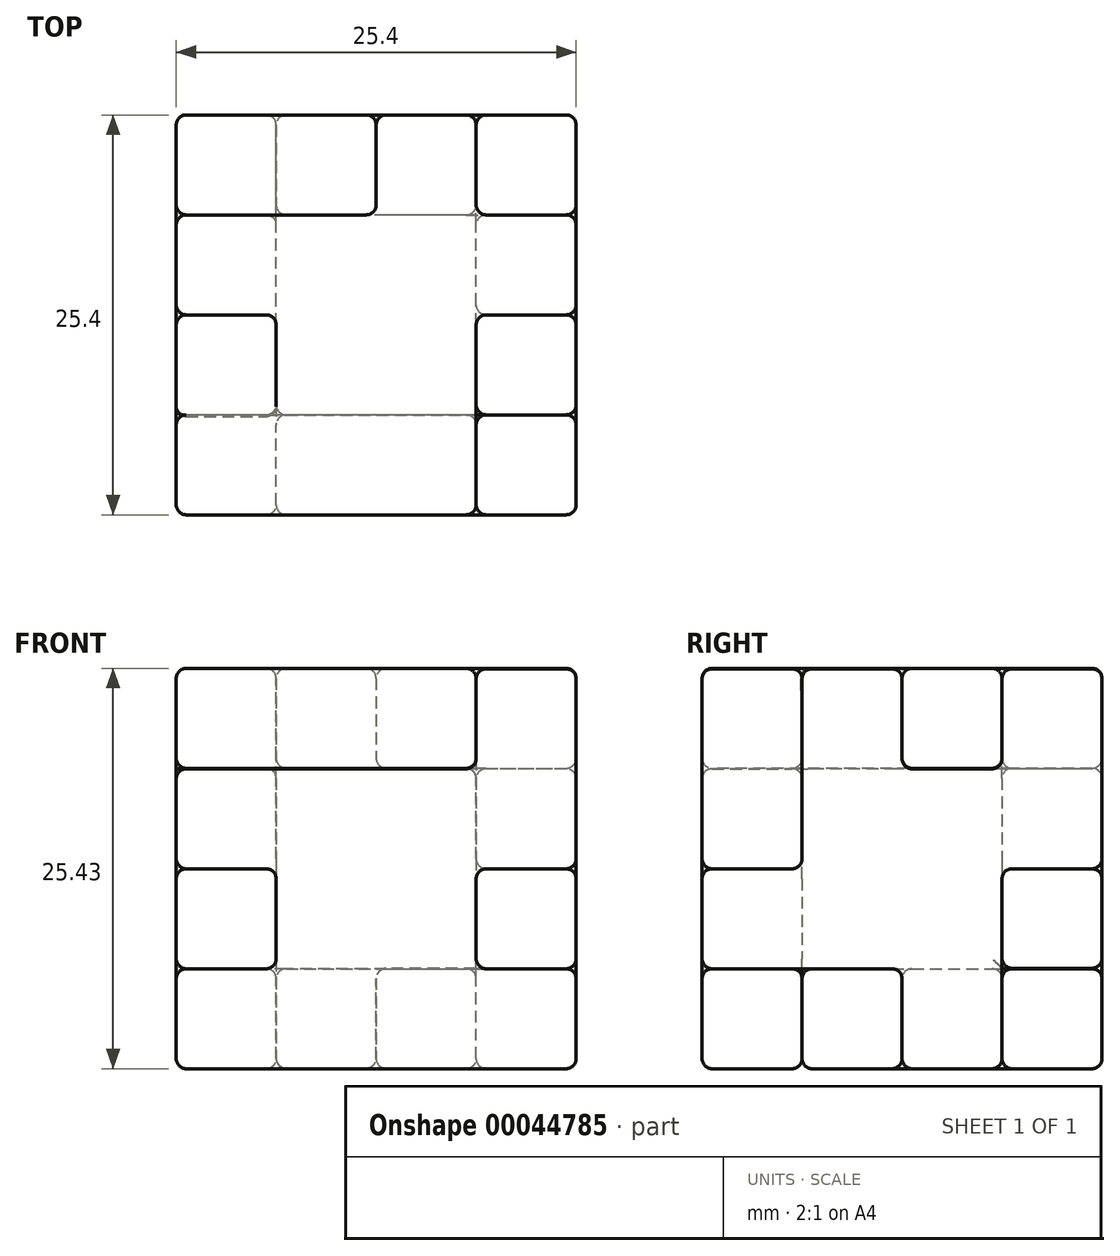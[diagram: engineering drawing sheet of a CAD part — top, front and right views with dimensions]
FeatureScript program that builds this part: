
annotation { "Feature Type Name" : "Feature", "Feature Type Description" : "" }
export const myFeature = defineFeature(function(context is Context, id is Id, definition is map)
    precondition{}
    {
        {
            var Q0;
            Q0=qCreatedBy(makeId("Front.planeOp"),FACE);
            var sketch = newSketch(context, id + "F0", { "sketchPlane" : qUnion([Q0])});
            skLineSegment(sketch, "E0", {"start": v(0, 12.73) * mm, "end": v(0, 6.38) * mm});
            skLineSegment(sketch, "E1.rect.bottom", {"start": v(6.35, 6.38) * mm, "end": v(0, 6.38) * mm});
            skLineSegment(sketch, "E1.rect.top", {"start": v(6.35, -6.32) * mm, "end": v(0, -6.32) * mm});
            skLineSegment(sketch, "E1.rect.left", {"start": v(6.35, 6.38) * mm, "end": v(6.35, 0) * mm});
            skLineSegment(sketch, "E1.rect.right", {"start": v(-6.35, 6.38) * mm, "end": v(-6.35, -6.32) * mm});
            skPoint(sketch, "E1.rect.middle", {"position": v(0, 0.03) * mm});
            skLineSegment(sketch, "E2", {"start": v(-6.35, 6.38) * mm, "end": v(-12.7, 6.38) * mm});
            skLineSegment(sketch, "E3", {"start": v(0, 6.38) * mm, "end": v(0, 12.73) * mm});
            skLineSegment(sketch, "E4", {"start": v(0, 12.73) * mm, "end": v(-12.67, 12.73) * mm});
            skLineSegment(sketch, "E5", {"start": v(-12.67, 12.73) * mm, "end": v(-12.7, 6.38) * mm});
            skLineSegment(sketch, "E6", {"start": v(6.35, -6.32) * mm, "end": v(12.7, -6.32) * mm});
            skLineSegment(sketch, "E7", {"start": v(12.7, 0) * mm, "end": v(12.7, -6.32) * mm});
            skLineSegment(sketch, "E8", {"start": v(12.7, 0) * mm, "end": v(6.35, 0) * mm});
            skLineSegment(sketch, "E9.trimOffspring", {"start": v(6.35, 0) * mm, "end": v(12.7, 0) * mm});
            skPoint(sketch, "E10.orphan", {"position": v(0, 22.29) * mm});
            skPoint(sketch, "E11.trimOffspring.end.orphan", {"position": v(0, -22.23) * mm});
            skPoint(sketch, "E12.start.orphan", {"position": v(-22.35, 0) * mm});
            skLineSegment(sketch, "E13", {"start": v(-6.35, -6.32) * mm, "end": v(-6.35, -12.67) * mm});
            skLineSegment(sketch, "E14", {"start": v(0, -6.32) * mm, "end": v(0, -12.67) * mm});
            skLineSegment(sketch, "E15", {"start": v(0, -12.67) * mm, "end": v(-6.35, -12.67) * mm});
            skSolve(sketch);
        }
        {
            var Q0;
            Q0 = qSketchRegion(id + "F0", true);
            extrude(context, id + "F1", {"entities" : qUnion([Q0]), "oppositeDirection" : true, "depth" : 6.35 * mm});
        }
        {
            var Q0;
            Q0=makeQuery(id+"F1.opExtrude","SWEPT_FACE",FACE,{"disambiguationData":[OSD([sQuery(id+"F0.wireOp",EDGE,"E1.rect.right"),sQuery(id+"F0.wireOp",EDGE,"E13")])]});
            var sketch = newSketch(context, id + "F2", { "sketchPlane" : qUnion([Q0])});
            skLineSegment(sketch, "E16", {"start": v(0, -12.67) * mm, "end": v(0, -6.32) * mm});
            skLineSegment(sketch, "E17.bottom", {"start": v(0, -6.32) * mm, "end": v(-6.35, -6.32) * mm});
            skLineSegment(sketch, "E17.top", {"start": v(0, 6.38) * mm, "end": v(-6.35, 6.38) * mm});
            skLineSegment(sketch, "E17.right", {"start": v(-6.35, -6.32) * mm, "end": v(-6.35, 6.38) * mm});
            skLineSegment(sketch, "E18", {"start": v(6.35, 6.38) * mm, "end": v(0, 6.38) * mm});
            skLineSegment(sketch, "E19", {"start": v(6.35, -6.35) * mm, "end": v(0, -6.35) * mm});
            skLineSegment(sketch, "E20.right", {"start": v(12.7, 0) * mm, "end": v(12.7, 6.35) * mm});
            skLineSegment(sketch, "E21", {"start": v(6.35, 6.38) * mm, "end": v(6.35, 12.73) * mm});
            skLineSegment(sketch, "E22", {"start": v(6.35, 12.73) * mm, "end": v(12.81, 12.73) * mm});
            skLineSegment(sketch, "E23", {"start": v(12.81, 12.73) * mm, "end": v(12.7, 6.35) * mm});
            skLineSegment(sketch, "E24", {"start": v(6.35, -12.7) * mm, "end": v(6.35, -6.35) * mm});
            skLineSegment(sketch, "E25", {"start": v(12.7, -12.7) * mm, "end": v(6.35, -12.7) * mm});
            skLineSegment(sketch, "E26", {"start": v(12.7, -6.35) * mm, "end": v(12.7, -12.7) * mm});
            skLineSegment(sketch, "E27", {"start": v(12.7, -6.35) * mm, "end": v(19.05, -6.35) * mm});
            skLineSegment(sketch, "E28", {"start": v(19.05, -6.35) * mm, "end": v(19.05, 0) * mm});
            skLineSegment(sketch, "E29", {"start": v(19.05, 0) * mm, "end": v(12.7, 0) * mm});
            skLineSegment(sketch, "E30", {"start": v(6.35, 6.38) * mm, "end": v(6.35, 6.35) * mm});
            skSolve(sketch);
        }
        {
            var Q0;
            Q0 = qSketchRegion(id + "F2", true);
            extrude(context, id + "F3", {"entities" : qUnion([Q0]), "depth" : 6.35 * mm});
        }
        {
            var Q0;
            Q0=makeQuery(id+"F3.opExtrude","SWEPT_FACE",FACE,{"disambiguationData":[OSD([sQuery(id+"F2.wireOp",EDGE,"E19")])]});
            var sketch = newSketch(context, id + "F4", { "sketchPlane" : qUnion([Q0])});
            skLineSegment(sketch, "E31", {"start": v(-12.7, 6.35) * mm, "end": v(-12.7, -6.35) * mm});
            skLineSegment(sketch, "E32", {"start": v(-12.7, -6.35) * mm, "end": v(-6.35, -6.35) * mm});
            skLineSegment(sketch, "E33", {"start": v(-6.35, -6.35) * mm, "end": v(-6.35, 0) * mm});
            skLineSegment(sketch, "E34", {"start": v(-6.35, 6.35) * mm, "end": v(-12.7, 6.35) * mm});
            skLineSegment(sketch, "E35", {"start": v(0, 0) * mm, "end": v(-6.35, 0) * mm});
            skLineSegment(sketch, "E36", {"start": v(-6.35, 0) * mm, "end": v(0, 0) * mm});
            skLineSegment(sketch, "E37", {"start": v(-6.35, 6.35) * mm, "end": v(-6.35, 12.7) * mm});
            skLineSegment(sketch, "E38", {"start": v(-6.35, 12.7) * mm, "end": v(12.7, 12.7) * mm});
            skLineSegment(sketch, "E39", {"start": v(12.7, 12.7) * mm, "end": v(12.7, 6.35) * mm});
            skLineSegment(sketch, "E40", {"start": v(12.7, 6.35) * mm, "end": v(6.35, 6.35) * mm});
            skLineSegment(sketch, "E41", {"start": v(6.35, 6.35) * mm, "end": v(6.35, 0) * mm});
            skLineSegment(sketch, "E42", {"start": v(6.35, 0) * mm, "end": v(12.7, 0) * mm});
            skLineSegment(sketch, "E43", {"start": v(0, 0) * mm, "end": v(0, -6.35) * mm});
            skLineSegment(sketch, "E44", {"start": v(0, -6.35) * mm, "end": v(12.7, -6.35) * mm});
            skLineSegment(sketch, "E45", {"start": v(12.7, -6.35) * mm, "end": v(12.7, 0) * mm});
            skPoint(sketch, "E46.start.orphan", {"position": v(0, 6.35) * mm});
            skLineSegment(sketch, "E47", {"start": v(-12.7, 6.35) * mm, "end": v(-6.35, 6.35) * mm, "construction": true});
            skLineSegment(sketch, "E48", {"start": v(-6.35, 0) * mm, "end": v(-6.35, -6.35) * mm, "construction": true});
            skSolve(sketch);
        }
        {
            var Q0;
            Q0 = qSketchRegion(id + "F4", true);
            extrude(context, id + "F5", {"entities" : qUnion([Q0]), "depth" : 6.35 * mm});
        }
        {
            var Q0;
            Q0=makeQuery(id+"F5.opExtrude","SWEPT_FACE",FACE,{"disambiguationData":[OSD([sQuery(id+"F4.wireOp",EDGE,"E41")])]});
            var sketch = newSketch(context, id + "F6", { "sketchPlane" : qUnion([Q0])});
            skLineSegment(sketch, "E49", {"start": v(0, -12.7) * mm, "end": v(-6.35, -12.7) * mm});
            skLineSegment(sketch, "E50", {"start": v(-6.35, -12.7) * mm, "end": v(-6.35, -6.35) * mm});
            skLineSegment(sketch, "E51", {"start": v(-6.35, -6.35) * mm, "end": v(-19.05, -6.35) * mm});
            skLineSegment(sketch, "E52", {"start": v(-19.05, -6.35) * mm, "end": v(-19.05, 0) * mm});
            skLineSegment(sketch, "E53", {"start": v(-19.05, 0) * mm, "end": v(-12.7, 0) * mm});
            skLineSegment(sketch, "E54", {"start": v(-12.7, 0) * mm, "end": v(-12.7, 12.7) * mm});
            skLineSegment(sketch, "E55", {"start": v(-12.7, 12.7) * mm, "end": v(-6.35, 12.7) * mm});
            skLineSegment(sketch, "E56", {"start": v(-6.35, 12.7) * mm, "end": v(-6.35, 6.35) * mm});
            skLineSegment(sketch, "E57", {"start": v(0, -12.7) * mm, "end": v(0, 0) * mm});
            skLineSegment(sketch, "E58", {"start": v(0, 0) * mm, "end": v(6.35, 0) * mm});
            skLineSegment(sketch, "E59", {"start": v(-6.35, 6.35) * mm, "end": v(0, 6.35) * mm});
            skLineSegment(sketch, "E60", {"start": v(0, 6.35) * mm, "end": v(0, 12.7) * mm});
            skLineSegment(sketch, "E61", {"start": v(6.35, 0) * mm, "end": v(6.35, 12.7) * mm});
            skLineSegment(sketch, "E62", {"start": v(6.35, 12.7) * mm, "end": v(0, 12.7) * mm});
            skSolve(sketch);
        }
        {
            var Q0;
            Q0 = qSketchRegion(id + "F6", true);
            extrude(context, id + "F7", {"entities" : qUnion([Q0]), "depth" : 6.35 * mm});
        }
        {
            var Q0;
            Q0=makeQuery(id+"F1.opExtrude","SWEPT_FACE",FACE,{"disambiguationData":[OSD([sQuery(id+"F0.wireOp",EDGE,"E1.rect.bottom")])]});
            var sketch = newSketch(context, id + "F8", { "sketchPlane" : qUnion([Q0])});
            skLineSegment(sketch, "E63", {"start": v(6.35, 6.35) * mm, "end": v(6.35, 0) * mm});
            skLineSegment(sketch, "E64", {"start": v(6.35, 0) * mm, "end": v(12.7, 0) * mm});
            skLineSegment(sketch, "E65", {"start": v(12.7, 0) * mm, "end": v(12.7, -6.35) * mm});
            skLineSegment(sketch, "E66", {"start": v(12.7, -6.35) * mm, "end": v(6.35, -6.35) * mm});
            skLineSegment(sketch, "E67", {"start": v(6.35, -6.35) * mm, "end": v(6.35, -19.05) * mm});
            skLineSegment(sketch, "E68", {"start": v(6.35, -19.05) * mm, "end": v(-12.7, -19.05) * mm});
            skLineSegment(sketch, "E69", {"start": v(-12.7, -19.05) * mm, "end": v(-12.7, -12.7) * mm});
            skLineSegment(sketch, "E70", {"start": v(-12.7, -12.7) * mm, "end": v(-6.35, -12.7) * mm});
            skLineSegment(sketch, "E71", {"start": v(-6.35, -12.7) * mm, "end": v(-6.35, -6.35) * mm});
            skLineSegment(sketch, "E72", {"start": v(-6.35, -6.35) * mm, "end": v(-12.7, -6.35) * mm});
            skLineSegment(sketch, "E73", {"start": v(-12.7, -6.35) * mm, "end": v(-12.7, 0) * mm});
            skLineSegment(sketch, "E74", {"start": v(-12.7, 0) * mm, "end": v(0, 0) * mm});
            skLineSegment(sketch, "E75", {"start": v(0, 0) * mm, "end": v(0, 6.35) * mm});
            skLineSegment(sketch, "E76", {"start": v(0, 6.35) * mm, "end": v(6.35, 6.35) * mm});
            skSolve(sketch);
        }
        {
            var Q0;
            Q0 = qSketchRegion(id + "F8", true);
            extrude(context, id + "F9", {"entities" : qUnion([Q0]), "depth" : 6.35 * mm});
        }
        {
            var Q0;
            Q0=makeQuery(id+"F5.opExtrude","SWEPT_FACE",FACE,{"disambiguationData":[OSD([sQuery(id+"F4.wireOp",EDGE,"E38")])]});
            var sketch = newSketch(context, id + "F10", { "sketchPlane" : qUnion([Q0])});
            skLineSegment(sketch, "E77", {"start": v(12.7, -12.7) * mm, "end": v(-12.7, -12.7) * mm});
            skLineSegment(sketch, "E78", {"start": v(12.7, -12.7) * mm, "end": v(12.7, -6.35) * mm});
            skLineSegment(sketch, "E79", {"start": v(12.7, -6.35) * mm, "end": v(6.35, -6.35) * mm});
            skLineSegment(sketch, "E80", {"start": v(6.35, -6.35) * mm, "end": v(6.35, 0) * mm});
            skLineSegment(sketch, "E81", {"start": v(6.35, 0) * mm, "end": v(12.7, 0) * mm});
            skLineSegment(sketch, "E82", {"start": v(12.7, 0) * mm, "end": v(12.7, 12.7) * mm});
            skLineSegment(sketch, "E83", {"start": v(12.7, 12.7) * mm, "end": v(6.35, 12.7) * mm});
            skLineSegment(sketch, "E84", {"start": v(6.35, 12.7) * mm, "end": v(6.35, 6.35) * mm});
            skLineSegment(sketch, "E85", {"start": v(6.35, 6.35) * mm, "end": v(-12.7, 6.35) * mm});
            skLineSegment(sketch, "E86", {"start": v(-12.7, 6.35) * mm, "end": v(-12.7, 0) * mm});
            skLineSegment(sketch, "E87", {"start": v(-12.7, 0) * mm, "end": v(-6.35, 0) * mm});
            skLineSegment(sketch, "E88", {"start": v(-6.35, 0) * mm, "end": v(-6.35, -6.35) * mm});
            skLineSegment(sketch, "E89", {"start": v(-6.35, -6.35) * mm, "end": v(-12.7, -6.35) * mm});
            skLineSegment(sketch, "E90", {"start": v(-12.7, -6.35) * mm, "end": v(-12.7, -12.7) * mm});
            skSolve(sketch);
        }
        {
            var Q0;
            Q0 = qSketchRegion(id + "F10", true);
            extrude(context, id + "F11", {"entities" : qUnion([Q0]), "depth" : 6.35 * mm});
        }
        {
            var Q0;
            Q0=makeQuery(id+"F1.opExtrude","CAP_FACE",FACE,{"disambiguationData":[OSD([sQuery(id+"F0.wireOp",EDGE,"E1.rect.bottom"),sQuery(id+"F0.wireOp",EDGE,"E1.rect.top"),sQuery(id+"F0.wireOp",EDGE,"E1.rect.left"),sQuery(id+"F0.wireOp",EDGE,"E1.rect.right"),sQuery(id+"F0.wireOp",EDGE,"E2"),sQuery(id+"F0.wireOp",EDGE,"E3"),sQuery(id+"F0.wireOp",EDGE,"E4"),sQuery(id+"F0.wireOp",EDGE,"E5"),sQuery(id+"F0.wireOp",EDGE,"E6"),sQuery(id+"F0.wireOp",EDGE,"E7"),sQuery(id+"F0.wireOp",EDGE,"E9.trimOffspring"),sQuery(id+"F0.wireOp",EDGE,"E13"),sQuery(id+"F0.wireOp",EDGE,"E14"),sQuery(id+"F0.wireOp",EDGE,"E15")])],"isStart":false});
            var Q1;
            Q1=makeQuery(id+"F1.opExtrude","CAP_FACE",FACE,{"disambiguationData":[OSD([sQuery(id+"F0.wireOp",EDGE,"E1.rect.bottom"),sQuery(id+"F0.wireOp",EDGE,"E1.rect.top"),sQuery(id+"F0.wireOp",EDGE,"E1.rect.left"),sQuery(id+"F0.wireOp",EDGE,"E1.rect.right"),sQuery(id+"F0.wireOp",EDGE,"E2"),sQuery(id+"F0.wireOp",EDGE,"E3"),sQuery(id+"F0.wireOp",EDGE,"E4"),sQuery(id+"F0.wireOp",EDGE,"E5"),sQuery(id+"F0.wireOp",EDGE,"E6"),sQuery(id+"F0.wireOp",EDGE,"E7"),sQuery(id+"F0.wireOp",EDGE,"E9.trimOffspring"),sQuery(id+"F0.wireOp",EDGE,"E13"),sQuery(id+"F0.wireOp",EDGE,"E14"),sQuery(id+"F0.wireOp",EDGE,"E15")])],"isStart":true});
            var Q2;
            Q2=makeQuery(id+"F1.opExtrude","SWEPT_EDGE",EDGE,{"disambiguationData":[OSD([sQuery(id+"F0.wireOp",EDGE,"E3"),sQuery(id+"F0.wireOp",EDGE,"E4")])]});
            var Q3;
            Q3=makeQuery(id+"F1.opExtrude","SWEPT_EDGE",EDGE,{"disambiguationData":[OSD([sQuery(id+"F0.wireOp",EDGE,"E1.rect.bottom"),sQuery(id+"F0.wireOp",EDGE,"E3")])]});
            var Q4;
            Q4=makeQuery(id+"F1.opExtrude","SWEPT_EDGE",EDGE,{"disambiguationData":[OSD([sQuery(id+"F0.wireOp",EDGE,"E1.rect.bottom"),sQuery(id+"F0.wireOp",EDGE,"E1.rect.left")])]});
            var Q5;
            Q5=makeQuery(id+"F1.opExtrude","SWEPT_EDGE",EDGE,{"disambiguationData":[OSD([sQuery(id+"F0.wireOp",EDGE,"E1.rect.left"),sQuery(id+"F0.wireOp",EDGE,"E9.trimOffspring")])]});
            var Q6;
            Q6=makeQuery(id+"F1.opExtrude","SWEPT_EDGE",EDGE,{"disambiguationData":[OSD([sQuery(id+"F0.wireOp",EDGE,"E7"),sQuery(id+"F0.wireOp",EDGE,"E9.trimOffspring")])]});
            var Q7;
            Q7=makeQuery(id+"F1.opExtrude","SWEPT_EDGE",EDGE,{"disambiguationData":[OSD([sQuery(id+"F0.wireOp",EDGE,"E6"),sQuery(id+"F0.wireOp",EDGE,"E7")])]});
            var Q8;
            Q8=makeQuery(id+"F1.opExtrude","SWEPT_EDGE",EDGE,{"disambiguationData":[OSD([sQuery(id+"F0.wireOp",EDGE,"E1.rect.top"),sQuery(id+"F0.wireOp",EDGE,"E14")])]});
            var Q9;
            Q9=makeQuery(id+"F1.opExtrude","SWEPT_EDGE",EDGE,{"disambiguationData":[OSD([sQuery(id+"F0.wireOp",EDGE,"E14"),sQuery(id+"F0.wireOp",EDGE,"E15")])]});
            var Q10;
            Q10=makeQuery(id+"F1.opExtrude","SWEPT_EDGE",EDGE,{"disambiguationData":[OSD([sQuery(id+"F0.wireOp",EDGE,"E13"),sQuery(id+"F0.wireOp",EDGE,"E15")])]});
            var Q11;
            Q11=makeQuery(id+"F1.opExtrude","SWEPT_EDGE",EDGE,{"disambiguationData":[OSD([sQuery(id+"F0.wireOp",EDGE,"E1.rect.right"),sQuery(id+"F0.wireOp",EDGE,"E2")])]});
            var Q12;
            Q12=makeQuery(id+"F1.opExtrude","SWEPT_EDGE",EDGE,{"disambiguationData":[OSD([sQuery(id+"F0.wireOp",EDGE,"E2"),sQuery(id+"F0.wireOp",EDGE,"E5")])]});
            var Q13;
            Q13=makeQuery(id+"F1.opExtrude","SWEPT_EDGE",EDGE,{"disambiguationData":[OSD([sQuery(id+"F0.wireOp",EDGE,"E4"),sQuery(id+"F0.wireOp",EDGE,"E5")])]});
            var Q14;
            Q14=makeQuery(id+"F3.opExtrude","CAP_FACE",FACE,{"disambiguationData":[OSD([sQuery(id+"F2.wireOp",EDGE,"E16"),sQuery(id+"F2.wireOp",EDGE,"E17.bottom"),sQuery(id+"F2.wireOp",EDGE,"E17.top"),sQuery(id+"F2.wireOp",EDGE,"E17.right"),sQuery(id+"F2.wireOp",EDGE,"E18"),sQuery(id+"F2.wireOp",EDGE,"E19"),sQuery(id+"F2.wireOp",EDGE,"E20.right"),sQuery(id+"F2.wireOp",EDGE,"E21"),sQuery(id+"F2.wireOp",EDGE,"E22"),sQuery(id+"F2.wireOp",EDGE,"E23"),sQuery(id+"F2.wireOp",EDGE,"E24"),sQuery(id+"F2.wireOp",EDGE,"E25"),sQuery(id+"F2.wireOp",EDGE,"E26"),sQuery(id+"F2.wireOp",EDGE,"E27"),sQuery(id+"F2.wireOp",EDGE,"E28"),sQuery(id+"F2.wireOp",EDGE,"E29")])],"isStart":false});
            var Q15;
            Q15=makeQuery(id+"F3.opExtrude","CAP_FACE",FACE,{"disambiguationData":[OSD([sQuery(id+"F2.wireOp",EDGE,"E16"),sQuery(id+"F2.wireOp",EDGE,"E17.bottom"),sQuery(id+"F2.wireOp",EDGE,"E17.top"),sQuery(id+"F2.wireOp",EDGE,"E17.right"),sQuery(id+"F2.wireOp",EDGE,"E18"),sQuery(id+"F2.wireOp",EDGE,"E19"),sQuery(id+"F2.wireOp",EDGE,"E20.right"),sQuery(id+"F2.wireOp",EDGE,"E21"),sQuery(id+"F2.wireOp",EDGE,"E22"),sQuery(id+"F2.wireOp",EDGE,"E23"),sQuery(id+"F2.wireOp",EDGE,"E24"),sQuery(id+"F2.wireOp",EDGE,"E25"),sQuery(id+"F2.wireOp",EDGE,"E26"),sQuery(id+"F2.wireOp",EDGE,"E27"),sQuery(id+"F2.wireOp",EDGE,"E28"),sQuery(id+"F2.wireOp",EDGE,"E29")])],"isStart":true});
            var Q16;
            Q16=makeQuery(id+"F3.opExtrude","SWEPT_EDGE",EDGE,{"disambiguationData":[OSD([sQuery(id+"F2.wireOp",EDGE,"E24"),sQuery(id+"F2.wireOp",EDGE,"E25")])]});
            var Q17;
            Q17=makeQuery(id+"F3.opExtrude","SWEPT_EDGE",EDGE,{"disambiguationData":[OSD([sQuery(id+"F2.wireOp",EDGE,"E25"),sQuery(id+"F2.wireOp",EDGE,"E26")])]});
            var Q18;
            Q18=makeQuery(id+"F3.opExtrude","SWEPT_EDGE",EDGE,{"disambiguationData":[OSD([sQuery(id+"F2.wireOp",EDGE,"E19"),sQuery(id+"F2.wireOp",EDGE,"E24")])]});
            var Q19;
            Q19=makeQuery(id+"F3.opExtrude","SWEPT_EDGE",EDGE,{"disambiguationData":[OSD([sQuery(id+"F0.wireOp",EDGE,"E1.rect.right"),sQuery(id+"F0.wireOp",EDGE,"E13"),sQuery(id+"F2.wireOp",EDGE,"E17.bottom"),sQuery(id+"F2.wireOp",EDGE,"E17.right")])]});
            var Q20;
            Q20=makeQuery(id+"F3.opExtrude","SWEPT_EDGE",EDGE,{"disambiguationData":[OSD([sQuery(id+"F2.wireOp",EDGE,"E17.top"),sQuery(id+"F2.wireOp",EDGE,"E17.right")])]});
            var Q21;
            Q21=makeQuery(id+"F3.opExtrude","SWEPT_EDGE",EDGE,{"disambiguationData":[OSD([sQuery(id+"F2.wireOp",EDGE,"E18"),sQuery(id+"F2.wireOp",EDGE,"E21")])]});
            var Q22;
            Q22=makeQuery(id+"F3.opExtrude","SWEPT_EDGE",EDGE,{"disambiguationData":[OSD([sQuery(id+"F2.wireOp",EDGE,"E21"),sQuery(id+"F2.wireOp",EDGE,"E22")])]});
            var Q23;
            Q23=makeQuery(id+"F3.opExtrude","SWEPT_EDGE",EDGE,{"disambiguationData":[OSD([sQuery(id+"F2.wireOp",EDGE,"E22"),sQuery(id+"F2.wireOp",EDGE,"E23")])]});
            var Q24;
            Q24=makeQuery(id+"F3.opExtrude","SWEPT_EDGE",EDGE,{"disambiguationData":[OSD([sQuery(id+"F2.wireOp",EDGE,"E28"),sQuery(id+"F2.wireOp",EDGE,"E29")])]});
            var Q25;
            Q25=makeQuery(id+"F3.opExtrude","SWEPT_EDGE",EDGE,{"disambiguationData":[OSD([sQuery(id+"F2.wireOp",EDGE,"E20.right"),sQuery(id+"F2.wireOp",EDGE,"E29")])]});
            var Q26;
            Q26=makeQuery(id+"F3.opExtrude","SWEPT_EDGE",EDGE,{"disambiguationData":[OSD([sQuery(id+"F2.wireOp",EDGE,"E27"),sQuery(id+"F2.wireOp",EDGE,"E28")])]});
            var Q27;
            Q27=makeQuery(id+"F3.opExtrude","SWEPT_EDGE",EDGE,{"disambiguationData":[OSD([sQuery(id+"F2.wireOp",EDGE,"E26"),sQuery(id+"F2.wireOp",EDGE,"E27")])]});
            var Q28;
            Q28=makeQuery(id+"F5.opExtrude","CAP_FACE",FACE,{"disambiguationData":[OSD([sQuery(id+"F4.wireOp",EDGE,"E31"),sQuery(id+"F4.wireOp",EDGE,"E32"),sQuery(id+"F4.wireOp",EDGE,"E33"),sQuery(id+"F4.wireOp",EDGE,"E34"),sQuery(id+"F4.wireOp",EDGE,"E36"),sQuery(id+"F4.wireOp",EDGE,"E37"),sQuery(id+"F4.wireOp",EDGE,"E38"),sQuery(id+"F4.wireOp",EDGE,"E39"),sQuery(id+"F4.wireOp",EDGE,"E40"),sQuery(id+"F4.wireOp",EDGE,"E41"),sQuery(id+"F4.wireOp",EDGE,"E42"),sQuery(id+"F4.wireOp",EDGE,"E43"),sQuery(id+"F4.wireOp",EDGE,"E44"),sQuery(id+"F4.wireOp",EDGE,"E45")])],"isStart":false});
            var Q29;
            Q29=makeQuery(id+"F5.opExtrude","CAP_FACE",FACE,{"disambiguationData":[OSD([sQuery(id+"F4.wireOp",EDGE,"E31"),sQuery(id+"F4.wireOp",EDGE,"E32"),sQuery(id+"F4.wireOp",EDGE,"E33"),sQuery(id+"F4.wireOp",EDGE,"E34"),sQuery(id+"F4.wireOp",EDGE,"E36"),sQuery(id+"F4.wireOp",EDGE,"E37"),sQuery(id+"F4.wireOp",EDGE,"E38"),sQuery(id+"F4.wireOp",EDGE,"E39"),sQuery(id+"F4.wireOp",EDGE,"E40"),sQuery(id+"F4.wireOp",EDGE,"E41"),sQuery(id+"F4.wireOp",EDGE,"E42"),sQuery(id+"F4.wireOp",EDGE,"E43"),sQuery(id+"F4.wireOp",EDGE,"E44"),sQuery(id+"F4.wireOp",EDGE,"E45")])],"isStart":true});
            var Q30;
            Q30=makeQuery(id+"F5.opExtrude","SWEPT_EDGE",EDGE,{"disambiguationData":[OSD([sQuery(id+"F4.wireOp",EDGE,"E32"),sQuery(id+"F4.wireOp",EDGE,"E33")])]});
            var Q31;
            Q31=makeQuery(id+"F5.opExtrude","SWEPT_EDGE",EDGE,{"disambiguationData":[OSD([sQuery(id+"F2.wireOp",EDGE,"E16"),sQuery(id+"F2.wireOp",EDGE,"E19"),sQuery(id+"F4.wireOp",EDGE,"E33"),sQuery(id+"F4.wireOp",EDGE,"E36")])]});
            var Q32;
            Q32=makeQuery(id+"F5.opExtrude","SWEPT_EDGE",EDGE,{"disambiguationData":[OSD([sQuery(id+"F4.wireOp",EDGE,"E31"),sQuery(id+"F4.wireOp",EDGE,"E32")])]});
            var Q33;
            Q33=makeQuery(id+"F5.opExtrude","SWEPT_EDGE",EDGE,{"disambiguationData":[OSD([sQuery(id+"F4.wireOp",EDGE,"E36"),sQuery(id+"F4.wireOp",EDGE,"E43")])]});
            var Q34;
            Q34=makeQuery(id+"F5.opExtrude","SWEPT_EDGE",EDGE,{"disambiguationData":[OSD([sQuery(id+"F4.wireOp",EDGE,"E43"),sQuery(id+"F4.wireOp",EDGE,"E44")])]});
            var Q35;
            Q35=makeQuery(id+"F5.opExtrude","SWEPT_EDGE",EDGE,{"disambiguationData":[OSD([sQuery(id+"F4.wireOp",EDGE,"E44"),sQuery(id+"F4.wireOp",EDGE,"E45")])]});
            var Q36;
            Q36=makeQuery(id+"F5.opExtrude","SWEPT_EDGE",EDGE,{"disambiguationData":[OSD([sQuery(id+"F4.wireOp",EDGE,"E42"),sQuery(id+"F4.wireOp",EDGE,"E45")])]});
            var Q37;
            Q37=makeQuery(id+"F5.opExtrude","SWEPT_EDGE",EDGE,{"disambiguationData":[OSD([sQuery(id+"F4.wireOp",EDGE,"E41"),sQuery(id+"F4.wireOp",EDGE,"E42")])]});
            var Q38;
            Q38=makeQuery(id+"F5.opExtrude","SWEPT_EDGE",EDGE,{"disambiguationData":[OSD([sQuery(id+"F4.wireOp",EDGE,"E40"),sQuery(id+"F4.wireOp",EDGE,"E41")])]});
            var Q39;
            Q39=makeQuery(id+"F5.opExtrude","SWEPT_EDGE",EDGE,{"disambiguationData":[OSD([sQuery(id+"F4.wireOp",EDGE,"E39"),sQuery(id+"F4.wireOp",EDGE,"E40")])]});
            var Q40;
            Q40=makeQuery(id+"F5.opExtrude","SWEPT_EDGE",EDGE,{"disambiguationData":[OSD([sQuery(id+"F4.wireOp",EDGE,"E38"),sQuery(id+"F4.wireOp",EDGE,"E39")])]});
            var Q41;
            Q41=makeQuery(id+"F5.opExtrude","SWEPT_EDGE",EDGE,{"disambiguationData":[OSD([sQuery(id+"F4.wireOp",EDGE,"E31"),sQuery(id+"F4.wireOp",EDGE,"E34")])]});
            var Q42;
            Q42=makeQuery(id+"F5.opExtrude","SWEPT_EDGE",EDGE,{"disambiguationData":[OSD([sQuery(id+"F2.wireOp",EDGE,"E19"),sQuery(id+"F4.wireOp",EDGE,"E34"),sQuery(id+"F4.wireOp",EDGE,"E37")])]});
            var Q43;
            Q43=makeQuery(id+"F5.opExtrude","SWEPT_EDGE",EDGE,{"disambiguationData":[OSD([sQuery(id+"F4.wireOp",EDGE,"E37"),sQuery(id+"F4.wireOp",EDGE,"E38")])]});
            var Q44;
            Q44=makeQuery(id+"F7.opExtrude","CAP_FACE",FACE,{"disambiguationData":[OSD([sQuery(id+"F6.wireOp",EDGE,"E49"),sQuery(id+"F6.wireOp",EDGE,"E50"),sQuery(id+"F6.wireOp",EDGE,"E51"),sQuery(id+"F6.wireOp",EDGE,"E52"),sQuery(id+"F6.wireOp",EDGE,"E53"),sQuery(id+"F6.wireOp",EDGE,"E54"),sQuery(id+"F6.wireOp",EDGE,"E55"),sQuery(id+"F6.wireOp",EDGE,"E56"),sQuery(id+"F6.wireOp",EDGE,"E57"),sQuery(id+"F6.wireOp",EDGE,"E58"),sQuery(id+"F6.wireOp",EDGE,"E59"),sQuery(id+"F6.wireOp",EDGE,"E60"),sQuery(id+"F6.wireOp",EDGE,"E61"),sQuery(id+"F6.wireOp",EDGE,"E62")])],"isStart":false});
            var Q45;
            Q45=makeQuery(id+"F7.opExtrude","CAP_FACE",FACE,{"disambiguationData":[OSD([sQuery(id+"F6.wireOp",EDGE,"E49"),sQuery(id+"F6.wireOp",EDGE,"E50"),sQuery(id+"F6.wireOp",EDGE,"E51"),sQuery(id+"F6.wireOp",EDGE,"E52"),sQuery(id+"F6.wireOp",EDGE,"E53"),sQuery(id+"F6.wireOp",EDGE,"E54"),sQuery(id+"F6.wireOp",EDGE,"E55"),sQuery(id+"F6.wireOp",EDGE,"E56"),sQuery(id+"F6.wireOp",EDGE,"E57"),sQuery(id+"F6.wireOp",EDGE,"E58"),sQuery(id+"F6.wireOp",EDGE,"E59"),sQuery(id+"F6.wireOp",EDGE,"E60"),sQuery(id+"F6.wireOp",EDGE,"E61"),sQuery(id+"F6.wireOp",EDGE,"E62")])],"isStart":true});
            var Q46;
            Q46=makeQuery(id+"F7.opExtrude","SWEPT_EDGE",EDGE,{"disambiguationData":[OSD([sQuery(id+"F6.wireOp",EDGE,"E56"),sQuery(id+"F6.wireOp",EDGE,"E59")])]});
            var Q47;
            Q47=makeQuery(id+"F7.opExtrude","SWEPT_EDGE",EDGE,{"disambiguationData":[OSD([sQuery(id+"F6.wireOp",EDGE,"E55"),sQuery(id+"F6.wireOp",EDGE,"E56")])]});
            var Q48;
            Q48=makeQuery(id+"F7.opExtrude","SWEPT_EDGE",EDGE,{"disambiguationData":[OSD([sQuery(id+"F6.wireOp",EDGE,"E54"),sQuery(id+"F6.wireOp",EDGE,"E55")])]});
            var Q49;
            Q49=makeQuery(id+"F7.opExtrude","SWEPT_EDGE",EDGE,{"disambiguationData":[OSD([sQuery(id+"F6.wireOp",EDGE,"E60"),sQuery(id+"F6.wireOp",EDGE,"E62")])]});
            var Q50;
            Q50=makeQuery(id+"F7.opExtrude","SWEPT_EDGE",EDGE,{"disambiguationData":[OSD([sQuery(id+"F6.wireOp",EDGE,"E61"),sQuery(id+"F6.wireOp",EDGE,"E62")])]});
            var Q51;
            Q51=makeQuery(id+"F7.opExtrude","SWEPT_EDGE",EDGE,{"disambiguationData":[OSD([sQuery(id+"F6.wireOp",EDGE,"E58"),sQuery(id+"F6.wireOp",EDGE,"E61")])]});
            var Q52;
            Q52=makeQuery(id+"F7.opExtrude","SWEPT_EDGE",EDGE,{"disambiguationData":[OSD([sQuery(id+"F6.wireOp",EDGE,"E59"),sQuery(id+"F6.wireOp",EDGE,"E60")])]});
            var Q53;
            Q53=makeQuery(id+"F7.opExtrude","SWEPT_EDGE",EDGE,{"disambiguationData":[OSD([sQuery(id+"F6.wireOp",EDGE,"E53"),sQuery(id+"F6.wireOp",EDGE,"E54")])]});
            var Q54;
            Q54=makeQuery(id+"F7.opExtrude","SWEPT_EDGE",EDGE,{"disambiguationData":[OSD([sQuery(id+"F6.wireOp",EDGE,"E52"),sQuery(id+"F6.wireOp",EDGE,"E53")])]});
            var Q55;
            Q55=makeQuery(id+"F7.opExtrude","SWEPT_EDGE",EDGE,{"disambiguationData":[OSD([sQuery(id+"F6.wireOp",EDGE,"E51"),sQuery(id+"F6.wireOp",EDGE,"E52")])]});
            var Q56;
            Q56=makeQuery(id+"F7.opExtrude","SWEPT_EDGE",EDGE,{"disambiguationData":[OSD([sQuery(id+"F6.wireOp",EDGE,"E57"),sQuery(id+"F6.wireOp",EDGE,"E58")])]});
            var Q57;
            Q57=makeQuery(id+"F7.opExtrude","SWEPT_EDGE",EDGE,{"disambiguationData":[OSD([sQuery(id+"F6.wireOp",EDGE,"E49"),sQuery(id+"F6.wireOp",EDGE,"E57")])]});
            var Q58;
            Q58=makeQuery(id+"F7.opExtrude","SWEPT_EDGE",EDGE,{"disambiguationData":[OSD([sQuery(id+"F6.wireOp",EDGE,"E49"),sQuery(id+"F6.wireOp",EDGE,"E50")])]});
            var Q59;
            Q59=makeQuery(id+"F7.opExtrude","SWEPT_EDGE",EDGE,{"disambiguationData":[OSD([sQuery(id+"F4.wireOp",EDGE,"E41"),sQuery(id+"F6.wireOp",EDGE,"E50"),sQuery(id+"F6.wireOp",EDGE,"E51")])]});
            var Q60;
            Q60=makeQuery(id+"F9.opExtrude","CAP_FACE",FACE,{"disambiguationData":[OSD([sQuery(id+"F8.wireOp",EDGE,"E63"),sQuery(id+"F8.wireOp",EDGE,"E64"),sQuery(id+"F8.wireOp",EDGE,"E65"),sQuery(id+"F8.wireOp",EDGE,"E66"),sQuery(id+"F8.wireOp",EDGE,"E67"),sQuery(id+"F8.wireOp",EDGE,"E68"),sQuery(id+"F8.wireOp",EDGE,"E69"),sQuery(id+"F8.wireOp",EDGE,"E70"),sQuery(id+"F8.wireOp",EDGE,"E71"),sQuery(id+"F8.wireOp",EDGE,"E72"),sQuery(id+"F8.wireOp",EDGE,"E73"),sQuery(id+"F8.wireOp",EDGE,"E74"),sQuery(id+"F8.wireOp",EDGE,"E75"),sQuery(id+"F8.wireOp",EDGE,"E76")])],"isStart":true});
            var Q61;
            Q61=makeQuery(id+"F9.opExtrude","CAP_FACE",FACE,{"disambiguationData":[OSD([sQuery(id+"F8.wireOp",EDGE,"E63"),sQuery(id+"F8.wireOp",EDGE,"E64"),sQuery(id+"F8.wireOp",EDGE,"E65"),sQuery(id+"F8.wireOp",EDGE,"E66"),sQuery(id+"F8.wireOp",EDGE,"E67"),sQuery(id+"F8.wireOp",EDGE,"E68"),sQuery(id+"F8.wireOp",EDGE,"E69"),sQuery(id+"F8.wireOp",EDGE,"E70"),sQuery(id+"F8.wireOp",EDGE,"E71"),sQuery(id+"F8.wireOp",EDGE,"E72"),sQuery(id+"F8.wireOp",EDGE,"E73"),sQuery(id+"F8.wireOp",EDGE,"E74"),sQuery(id+"F8.wireOp",EDGE,"E75"),sQuery(id+"F8.wireOp",EDGE,"E76")])],"isStart":false});
            var Q62;
            Q62=makeQuery(id+"F9.opExtrude","SWEPT_EDGE",EDGE,{"disambiguationData":[OSD([sQuery(id+"F8.wireOp",EDGE,"E70"),sQuery(id+"F8.wireOp",EDGE,"E71")])]});
            var Q63;
            Q63=makeQuery(id+"F9.opExtrude","SWEPT_EDGE",EDGE,{"disambiguationData":[OSD([sQuery(id+"F8.wireOp",EDGE,"E69"),sQuery(id+"F8.wireOp",EDGE,"E70")])]});
            var Q64;
            Q64=makeQuery(id+"F9.opExtrude","SWEPT_EDGE",EDGE,{"disambiguationData":[OSD([sQuery(id+"F8.wireOp",EDGE,"E72"),sQuery(id+"F8.wireOp",EDGE,"E73")])]});
            var Q65;
            Q65=makeQuery(id+"F9.opExtrude","SWEPT_EDGE",EDGE,{"disambiguationData":[OSD([sQuery(id+"F8.wireOp",EDGE,"E73"),sQuery(id+"F8.wireOp",EDGE,"E74")])]});
            var Q66;
            Q66=makeQuery(id+"F9.opExtrude","SWEPT_EDGE",EDGE,{"disambiguationData":[OSD([sQuery(id+"F0.wireOp",EDGE,"E1.rect.bottom"),sQuery(id+"F8.wireOp",EDGE,"E74"),sQuery(id+"F8.wireOp",EDGE,"E75")])]});
            var Q67;
            Q67=makeQuery(id+"F9.opExtrude","SWEPT_EDGE",EDGE,{"disambiguationData":[OSD([sQuery(id+"F8.wireOp",EDGE,"E75"),sQuery(id+"F8.wireOp",EDGE,"E76")])]});
            var Q68;
            Q68=makeQuery(id+"F9.opExtrude","SWEPT_EDGE",EDGE,{"disambiguationData":[OSD([sQuery(id+"F8.wireOp",EDGE,"E63"),sQuery(id+"F8.wireOp",EDGE,"E76")])]});
            var Q69;
            Q69=makeQuery(id+"F9.opExtrude","SWEPT_EDGE",EDGE,{"disambiguationData":[OSD([sQuery(id+"F0.wireOp",EDGE,"E1.rect.bottom"),sQuery(id+"F8.wireOp",EDGE,"E63"),sQuery(id+"F8.wireOp",EDGE,"E64")])]});
            var Q70;
            Q70=makeQuery(id+"F9.opExtrude","SWEPT_EDGE",EDGE,{"disambiguationData":[OSD([sQuery(id+"F8.wireOp",EDGE,"E64"),sQuery(id+"F8.wireOp",EDGE,"E65")])]});
            var Q71;
            Q71=makeQuery(id+"F9.opExtrude","SWEPT_EDGE",EDGE,{"disambiguationData":[OSD([sQuery(id+"F8.wireOp",EDGE,"E65"),sQuery(id+"F8.wireOp",EDGE,"E66")])]});
            var Q72;
            Q72=makeQuery(id+"F9.opExtrude","SWEPT_EDGE",EDGE,{"disambiguationData":[OSD([sQuery(id+"F8.wireOp",EDGE,"E66"),sQuery(id+"F8.wireOp",EDGE,"E67")])]});
            var Q73;
            Q73=makeQuery(id+"F9.opExtrude","SWEPT_EDGE",EDGE,{"disambiguationData":[OSD([sQuery(id+"F8.wireOp",EDGE,"E67"),sQuery(id+"F8.wireOp",EDGE,"E68")])]});
            var Q74;
            Q74=makeQuery(id+"F9.opExtrude","SWEPT_EDGE",EDGE,{"disambiguationData":[OSD([sQuery(id+"F8.wireOp",EDGE,"E68"),sQuery(id+"F8.wireOp",EDGE,"E69")])]});
            var Q75;
            Q75=makeQuery(id+"F9.opExtrude","SWEPT_EDGE",EDGE,{"disambiguationData":[OSD([sQuery(id+"F8.wireOp",EDGE,"E71"),sQuery(id+"F8.wireOp",EDGE,"E72")])]});
            var Q76;
            Q76=makeQuery(id+"F11.opExtrude","CAP_FACE",FACE,{"disambiguationData":[OSD([sQuery(id+"F10.wireOp",EDGE,"E77"),sQuery(id+"F10.wireOp",EDGE,"E78"),sQuery(id+"F10.wireOp",EDGE,"E79"),sQuery(id+"F10.wireOp",EDGE,"E80"),sQuery(id+"F10.wireOp",EDGE,"E81"),sQuery(id+"F10.wireOp",EDGE,"E82"),sQuery(id+"F10.wireOp",EDGE,"E83"),sQuery(id+"F10.wireOp",EDGE,"E84"),sQuery(id+"F10.wireOp",EDGE,"E85"),sQuery(id+"F10.wireOp",EDGE,"E86"),sQuery(id+"F10.wireOp",EDGE,"E87"),sQuery(id+"F10.wireOp",EDGE,"E88"),sQuery(id+"F10.wireOp",EDGE,"E89"),sQuery(id+"F10.wireOp",EDGE,"E90")])],"isStart":false});
            var Q77;
            Q77=makeQuery(id+"F11.opExtrude","CAP_FACE",FACE,{"disambiguationData":[OSD([sQuery(id+"F10.wireOp",EDGE,"E77"),sQuery(id+"F10.wireOp",EDGE,"E78"),sQuery(id+"F10.wireOp",EDGE,"E79"),sQuery(id+"F10.wireOp",EDGE,"E80"),sQuery(id+"F10.wireOp",EDGE,"E81"),sQuery(id+"F10.wireOp",EDGE,"E82"),sQuery(id+"F10.wireOp",EDGE,"E83"),sQuery(id+"F10.wireOp",EDGE,"E84"),sQuery(id+"F10.wireOp",EDGE,"E85"),sQuery(id+"F10.wireOp",EDGE,"E86"),sQuery(id+"F10.wireOp",EDGE,"E87"),sQuery(id+"F10.wireOp",EDGE,"E88"),sQuery(id+"F10.wireOp",EDGE,"E89"),sQuery(id+"F10.wireOp",EDGE,"E90")])],"isStart":true});
            var Q78;
            Q78=makeQuery(id+"F11.opExtrude","SWEPT_EDGE",EDGE,{"disambiguationData":[OSD([sQuery(id+"F10.wireOp",EDGE,"E83"),sQuery(id+"F10.wireOp",EDGE,"E84")])]});
            var Q79;
            Q79=makeQuery(id+"F11.opExtrude","SWEPT_EDGE",EDGE,{"disambiguationData":[OSD([sQuery(id+"F10.wireOp",EDGE,"E84"),sQuery(id+"F10.wireOp",EDGE,"E85")])]});
            var Q80;
            Q80=makeQuery(id+"F11.opExtrude","SWEPT_EDGE",EDGE,{"disambiguationData":[OSD([sQuery(id+"F10.wireOp",EDGE,"E85"),sQuery(id+"F10.wireOp",EDGE,"E86")])]});
            var Q81;
            Q81=makeQuery(id+"F11.opExtrude","SWEPT_EDGE",EDGE,{"disambiguationData":[OSD([sQuery(id+"F10.wireOp",EDGE,"E86"),sQuery(id+"F10.wireOp",EDGE,"E87")])]});
            var Q82;
            Q82=makeQuery(id+"F11.opExtrude","SWEPT_EDGE",EDGE,{"disambiguationData":[OSD([sQuery(id+"F10.wireOp",EDGE,"E89"),sQuery(id+"F10.wireOp",EDGE,"E90")])]});
            var Q83;
            Q83=makeQuery(id+"F11.opExtrude","SWEPT_EDGE",EDGE,{"disambiguationData":[OSD([sQuery(id+"F4.wireOp",EDGE,"E37"),sQuery(id+"F4.wireOp",EDGE,"E38"),sQuery(id+"F10.wireOp",EDGE,"E88"),sQuery(id+"F10.wireOp",EDGE,"E89")])]});
            var Q84;
            Q84=makeQuery(id+"F11.opExtrude","SWEPT_EDGE",EDGE,{"disambiguationData":[OSD([sQuery(id+"F10.wireOp",EDGE,"E77"),sQuery(id+"F10.wireOp",EDGE,"E90")])]});
            var Q85;
            Q85=makeQuery(id+"F11.opExtrude","SWEPT_EDGE",EDGE,{"disambiguationData":[OSD([sQuery(id+"F10.wireOp",EDGE,"E87"),sQuery(id+"F10.wireOp",EDGE,"E88")])]});
            var Q86;
            Q86=makeQuery(id+"F11.opExtrude","SWEPT_EDGE",EDGE,{"disambiguationData":[OSD([sQuery(id+"F10.wireOp",EDGE,"E78"),sQuery(id+"F10.wireOp",EDGE,"E79")])]});
            var Q87;
            Q87=makeQuery(id+"F11.opExtrude","SWEPT_EDGE",EDGE,{"disambiguationData":[OSD([sQuery(id+"F10.wireOp",EDGE,"E77"),sQuery(id+"F10.wireOp",EDGE,"E78")])]});
            var Q88;
            Q88=makeQuery(id+"F11.opExtrude","SWEPT_EDGE",EDGE,{"disambiguationData":[OSD([sQuery(id+"F10.wireOp",EDGE,"E81"),sQuery(id+"F10.wireOp",EDGE,"E82")])]});
            var Q89;
            Q89=makeQuery(id+"F11.opExtrude","SWEPT_EDGE",EDGE,{"disambiguationData":[OSD([sQuery(id+"F10.wireOp",EDGE,"E82"),sQuery(id+"F10.wireOp",EDGE,"E83")])]});
            var Q90;
            Q90=makeQuery(id+"F11.opExtrude","SWEPT_EDGE",EDGE,{"disambiguationData":[OSD([sQuery(id+"F10.wireOp",EDGE,"E80"),sQuery(id+"F10.wireOp",EDGE,"E81")])]});
            var Q91;
            Q91=makeQuery(id+"F11.opExtrude","SWEPT_EDGE",EDGE,{"disambiguationData":[OSD([sQuery(id+"F4.wireOp",EDGE,"E38"),sQuery(id+"F10.wireOp",EDGE,"E79"),sQuery(id+"F10.wireOp",EDGE,"E80")])]});
            fillet(context, id + "F12", {"entities" : qUnion([Q0, Q1, Q2, Q3, Q4, Q5, Q6, Q7, Q8, Q9, Q10, Q11, Q12, Q13, Q14, Q15, Q16, Q17, Q18, Q19, Q20, Q21, Q22, Q23, Q24, Q25, Q26, Q27, Q28, Q29, Q30, Q31, Q32, Q33, Q34, Q35, Q36, Q37, Q38, Q39, Q40, Q41, Q42, Q43, Q44, Q45, Q46, Q47, Q48, Q49, Q50, Q51, Q52, Q53, Q54, Q55, Q56, Q57, Q58, Q59, Q60, Q61, Q62, Q63, Q64, Q65, Q66, Q67, Q68, Q69, Q70, Q71, Q72, Q73, Q74, Q75, Q76, Q77, Q78, Q79, Q80, Q81, Q82, Q83, Q84, Q85, Q86, Q87, Q88, Q89, Q90, Q91]), "radius" : 0.64 * mm, "tangentPropagation" : true, "allowEdgeOverflow" : false});
        }
        {
            var Q0;
            Q0=makeQuery(id+"F1.opExtrude","SWEPT_BODY",BODY,{"disambiguationData":[OSD([sQuery(id+"F0.wireOp",EDGE,"E1.rect.bottom"),sQuery(id+"F0.wireOp",EDGE,"E1.rect.top"),sQuery(id+"F0.wireOp",EDGE,"E1.rect.left"),sQuery(id+"F0.wireOp",EDGE,"E1.rect.right"),sQuery(id+"F0.wireOp",EDGE,"E2"),sQuery(id+"F0.wireOp",EDGE,"E3"),sQuery(id+"F0.wireOp",EDGE,"E4"),sQuery(id+"F0.wireOp",EDGE,"E5"),sQuery(id+"F0.wireOp",EDGE,"E6"),sQuery(id+"F0.wireOp",EDGE,"E7"),sQuery(id+"F0.wireOp",EDGE,"E9.trimOffspring"),sQuery(id+"F0.wireOp",EDGE,"E13"),sQuery(id+"F0.wireOp",EDGE,"E14"),sQuery(id+"F0.wireOp",EDGE,"E15")])]});
            var Q1;
            Q1=makeQuery(id+"F3.opExtrude","SWEPT_BODY",BODY,{"disambiguationData":[OSD([sQuery(id+"F2.wireOp",EDGE,"E16"),sQuery(id+"F2.wireOp",EDGE,"E17.bottom"),sQuery(id+"F2.wireOp",EDGE,"E17.top"),sQuery(id+"F2.wireOp",EDGE,"E17.right"),sQuery(id+"F2.wireOp",EDGE,"E18"),sQuery(id+"F2.wireOp",EDGE,"E19"),sQuery(id+"F2.wireOp",EDGE,"E20.right"),sQuery(id+"F2.wireOp",EDGE,"E21"),sQuery(id+"F2.wireOp",EDGE,"E22"),sQuery(id+"F2.wireOp",EDGE,"E23"),sQuery(id+"F2.wireOp",EDGE,"E24"),sQuery(id+"F2.wireOp",EDGE,"E25"),sQuery(id+"F2.wireOp",EDGE,"E26"),sQuery(id+"F2.wireOp",EDGE,"E27"),sQuery(id+"F2.wireOp",EDGE,"E28"),sQuery(id+"F2.wireOp",EDGE,"E29")])]});
            var Q2;
            Q2=makeQuery(id+"F5.opExtrude","SWEPT_BODY",BODY,{"disambiguationData":[OSD([sQuery(id+"F4.wireOp",EDGE,"E31"),sQuery(id+"F4.wireOp",EDGE,"E32"),sQuery(id+"F4.wireOp",EDGE,"E33"),sQuery(id+"F4.wireOp",EDGE,"E34"),sQuery(id+"F4.wireOp",EDGE,"E36"),sQuery(id+"F4.wireOp",EDGE,"E37"),sQuery(id+"F4.wireOp",EDGE,"E38"),sQuery(id+"F4.wireOp",EDGE,"E39"),sQuery(id+"F4.wireOp",EDGE,"E40"),sQuery(id+"F4.wireOp",EDGE,"E41"),sQuery(id+"F4.wireOp",EDGE,"E42"),sQuery(id+"F4.wireOp",EDGE,"E43"),sQuery(id+"F4.wireOp",EDGE,"E44"),sQuery(id+"F4.wireOp",EDGE,"E45")])]});
            var Q3;
            Q3=makeQuery(id+"F7.opExtrude","SWEPT_BODY",BODY,{"disambiguationData":[OSD([sQuery(id+"F6.wireOp",EDGE,"E49"),sQuery(id+"F6.wireOp",EDGE,"E50"),sQuery(id+"F6.wireOp",EDGE,"E51"),sQuery(id+"F6.wireOp",EDGE,"E52"),sQuery(id+"F6.wireOp",EDGE,"E53"),sQuery(id+"F6.wireOp",EDGE,"E54"),sQuery(id+"F6.wireOp",EDGE,"E55"),sQuery(id+"F6.wireOp",EDGE,"E56"),sQuery(id+"F6.wireOp",EDGE,"E57"),sQuery(id+"F6.wireOp",EDGE,"E58"),sQuery(id+"F6.wireOp",EDGE,"E59"),sQuery(id+"F6.wireOp",EDGE,"E60"),sQuery(id+"F6.wireOp",EDGE,"E61"),sQuery(id+"F6.wireOp",EDGE,"E62")])]});
            var Q4;
            Q4=makeQuery(id+"F9.opExtrude","SWEPT_BODY",BODY,{"disambiguationData":[OSD([sQuery(id+"F8.wireOp",EDGE,"E63"),sQuery(id+"F8.wireOp",EDGE,"E64"),sQuery(id+"F8.wireOp",EDGE,"E65"),sQuery(id+"F8.wireOp",EDGE,"E66"),sQuery(id+"F8.wireOp",EDGE,"E67"),sQuery(id+"F8.wireOp",EDGE,"E68"),sQuery(id+"F8.wireOp",EDGE,"E69"),sQuery(id+"F8.wireOp",EDGE,"E70"),sQuery(id+"F8.wireOp",EDGE,"E71"),sQuery(id+"F8.wireOp",EDGE,"E72"),sQuery(id+"F8.wireOp",EDGE,"E73"),sQuery(id+"F8.wireOp",EDGE,"E74"),sQuery(id+"F8.wireOp",EDGE,"E75"),sQuery(id+"F8.wireOp",EDGE,"E76")])]});
            var Q5;
            Q5=makeQuery(id+"F11.opExtrude","SWEPT_BODY",BODY,{"disambiguationData":[OSD([sQuery(id+"F10.wireOp",EDGE,"E77"),sQuery(id+"F10.wireOp",EDGE,"E78"),sQuery(id+"F10.wireOp",EDGE,"E79"),sQuery(id+"F10.wireOp",EDGE,"E80"),sQuery(id+"F10.wireOp",EDGE,"E81"),sQuery(id+"F10.wireOp",EDGE,"E82"),sQuery(id+"F10.wireOp",EDGE,"E83"),sQuery(id+"F10.wireOp",EDGE,"E84"),sQuery(id+"F10.wireOp",EDGE,"E85"),sQuery(id+"F10.wireOp",EDGE,"E86"),sQuery(id+"F10.wireOp",EDGE,"E87"),sQuery(id+"F10.wireOp",EDGE,"E88"),sQuery(id+"F10.wireOp",EDGE,"E89"),sQuery(id+"F10.wireOp",EDGE,"E90")])]});
            transform(context, id + "F13", {"entities" : qUnion([Q0, Q1, Q2, Q3, Q4, Q5]), "transformType" : TransformType.TRANSLATION_3D, "dx" : 0 * mm, "dy" : 6.35 * mm, "dz" : 0 * mm, "makeCopy" : false});
        }
    });
